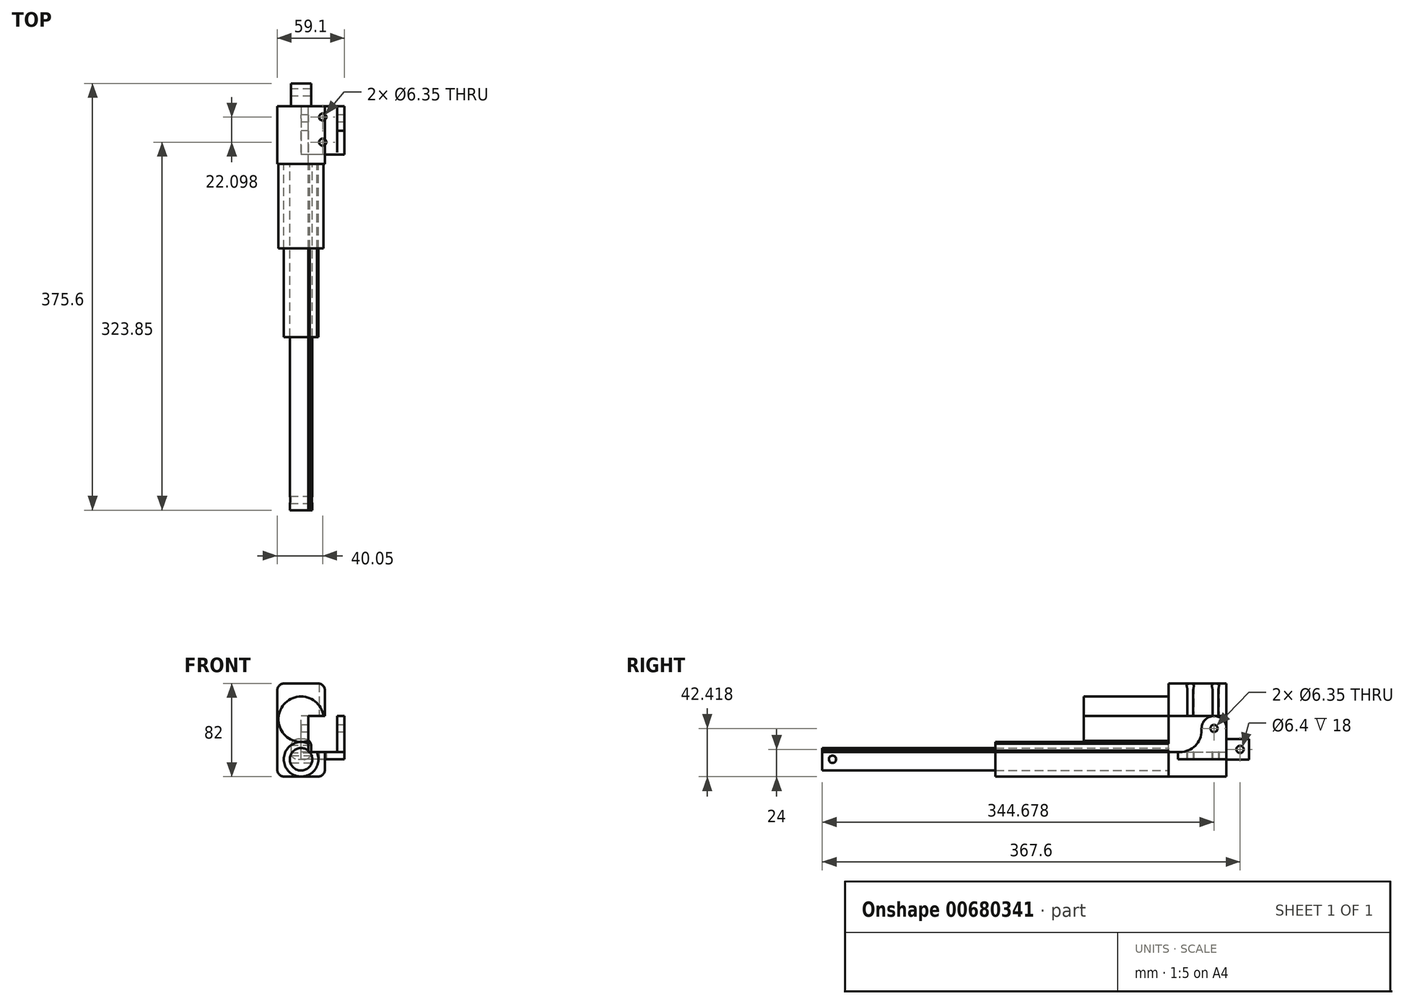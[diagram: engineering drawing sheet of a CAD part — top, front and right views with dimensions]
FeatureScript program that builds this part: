
annotation { "Feature Type Name" : "Feature", "Feature Type Description" : "" }
export const myFeature = defineFeature(function(context is Context, id is Id, definition is map)
    precondition{}
    {
        {
            var Q0;
            Q0=qCreatedBy(makeId("Front.planeOp"),FACE);
            var sketch = newSketch(context, id + "F0", { "sketchPlane" : qUnion([Q0])});
            skCircle(sketch, "E0", {"center": v(0, 0) * mm, "radius": 15.24 * mm});
            skCircle(sketch, "E1", {"center": v(0, 0) * mm, "radius": 9.9 * mm});
            skSolve(sketch);
        }
        {
            var Q0;
            Q0 = qSketchRegion(id + "F0", true);
            extrude(context, id + "F1", {"entities" : qUnion([Q0]), "depth" : 203.2 * mm, "offsetDistance" : 25.4 * mm});
        }
        {
            var Q0;
            Q0=makeQuery(id+"F1.opExtrude","CAP_FACE",FACE,{"disambiguationData":[OSD([sQuery(id+"F0.wireOp",EDGE,"E0"),sQuery(id+"F0.wireOp",EDGE,"E1")])],"isStart":true});
            var sketch = newSketch(context, id + "F2", { "sketchPlane" : qUnion([Q0])});
            skLineSegment(sketch, "E2.bottom", {"start": v(-14.65, 66.76) * mm, "end": v(14.65, 66.76) * mm});
            skLineSegment(sketch, "E2.top", {"start": v(-14.65, -15.24) * mm, "end": v(14.65, -15.24) * mm});
            skLineSegment(sketch, "E2.left", {"start": v(-21, 60.4) * mm, "end": v(-21, -8.89) * mm});
            skLineSegment(sketch, "E2.right", {"start": v(21, 60.4) * mm, "end": v(21, -8.9) * mm});
            skPoint(sketch, "E3", {"position": v(0, 66.76) * mm});
            skPoint(sketch, "E4.visualSharp", {"position": v(-21, -15.24) * mm});
            skArc(sketch, "E4.filletArc", {"start": v(-21, -8.9) * mm, "mid": v(-19.14, -13.38) * mm, "end": v(-14.65, -15.24) * mm});
            skPoint(sketch, "E5.visualSharp", {"position": v(21, -15.24) * mm});
            skArc(sketch, "E5.filletArc", {"start": v(14.65, -15.24) * mm, "mid": v(19.14, -13.38) * mm, "end": v(21, -8.9) * mm});
            skPoint(sketch, "E6.visualSharp", {"position": v(21, 66.76) * mm});
            skArc(sketch, "E6.filletArc", {"start": v(21, 60.4) * mm, "mid": v(19.14, 64.9) * mm, "end": v(14.65, 66.76) * mm});
            skPoint(sketch, "E7.visualSharp", {"position": v(-21, 66.76) * mm});
            skArc(sketch, "E7.filletArc", {"start": v(-14.65, 66.76) * mm, "mid": v(-19.14, 64.9) * mm, "end": v(-21, 60.4) * mm});
            skSolve(sketch);
        }
        {
            var Q0;
            Q0 = qSketchRegion(id + "F2", true);
            extrude(context, id + "F3", {"entities" : qUnion([Q0]), "operationType" : NewBodyOperationType.ADD, "oppositeDirection" : true, "depth" : 50.8 * mm, "offsetDistance" : 25.4 * mm});
        }
        {
            var Q0;
            Q0=makeQuery(id+"F3.boolean.opBoolean","MERGE",FACE,{"derivedFrom":[makeQuery(id+"F1.opExtrude","CAP_FACE",FACE,{"disambiguationData":[OSD([sQuery(id+"F0.wireOp",EDGE,"E0"),sQuery(id+"F0.wireOp",EDGE,"E1")])],"isStart":true}),makeQuery(id+"F3.opExtrude","CAP_FACE",FACE,{"disambiguationData":[OSD([sQuery(id+"F2.wireOp",EDGE,"E2.bottom"),sQuery(id+"F2.wireOp",EDGE,"E2.top"),sQuery(id+"F2.wireOp",EDGE,"E2.left"),sQuery(id+"F2.wireOp",EDGE,"E2.right")])],"isStart":true})]});
            var sketch = newSketch(context, id + "F4", { "sketchPlane" : qUnion([Q0])});
            skLineSegment(sketch, "E8", {"start": v(0, -15.24) * mm, "end": v(0, 66.76) * mm, "construction": true});
            skLineSegment(sketch, "E9.bottom", {"start": v(-2.65, 17.76) * mm, "end": v(2.65, 17.76) * mm});
            skLineSegment(sketch, "E9.top", {"start": v(-2.65, -0.24) * mm, "end": v(2.65, -0.24) * mm});
            skLineSegment(sketch, "E9.left", {"start": v(-9, 11.41) * mm, "end": v(-9, 6.11) * mm});
            skLineSegment(sketch, "E9.right", {"start": v(9, 11.41) * mm, "end": v(9, 6.11) * mm});
            skPoint(sketch, "E10", {"position": v(0, 17.76) * mm});
            skPoint(sketch, "E11", {"position": v(-9, 8.76) * mm});
            skPoint(sketch, "E12.visualSharp", {"position": v(-9, 17.76) * mm});
            skArc(sketch, "E12.filletArc", {"start": v(-2.65, 17.76) * mm, "mid": v(-7.14, 15.9) * mm, "end": v(-9, 11.41) * mm});
            skPoint(sketch, "E13.visualSharp", {"position": v(9, 17.76) * mm});
            skArc(sketch, "E13.filletArc", {"start": v(9, 11.41) * mm, "mid": v(7.14, 15.9) * mm, "end": v(2.65, 17.76) * mm});
            skPoint(sketch, "E14.visualSharp", {"position": v(9, -0.24) * mm});
            skArc(sketch, "E14.filletArc", {"start": v(2.65, -0.24) * mm, "mid": v(7.14, 1.62) * mm, "end": v(9, 6.11) * mm});
            skPoint(sketch, "E15.visualSharp", {"position": v(-9, -0.24) * mm});
            skArc(sketch, "E15.filletArc", {"start": v(-9, 6.11) * mm, "mid": v(-7.14, 1.62) * mm, "end": v(-2.65, -0.24) * mm});
            skSolve(sketch);
        }
        {
            var Q0;
            Q0 = qSketchRegion(id + "F4", true);
            extrude(context, id + "F5", {"entities" : qUnion([Q0]), "operationType" : NewBodyOperationType.ADD, "depth" : 20 * mm, "offsetDistance" : 25.4 * mm});
        }
        {
            var Q0;
            Q0=makeQuery(id+"F1.opExtrude","CAP_FACE",FACE,{"disambiguationData":[OSD([sQuery(id+"F0.wireOp",EDGE,"E0"),sQuery(id+"F0.wireOp",EDGE,"E1")])],"isStart":false});
            var sketch = newSketch(context, id + "F6", { "sketchPlane" : qUnion([Q0])});
            skCircle(sketch, "E16", {"center": v(0, 0) * mm, "radius": 9.9 * mm});
            skSolve(sketch);
        }
        {
            var Q0;
            Q0 = qSketchRegion(id + "F6", true);
            extrude(context, id + "F7", {"entities" : qUnion([Q0]), "depth" : 152.4 * mm, "offsetDistance" : 25.4 * mm});
        }
        {
            var Q0;
            {var subQ0=sQuery(id+"F2.wireOp",EDGE,"E2.left");var subQ1=sQuery(id+"F2.wireOp",EDGE,"E2.top");var subQ2=sQuery(id+"F2.wireOp",EDGE,"E2.bottom");var subQ3=sQuery(id+"F2.wireOp",EDGE,"E2.right");var subQ4=sQuery(id+"F2.wireOp",EDGE,"E4.filletArc");var subQ5=sQuery(id+"F2.wireOp",EDGE,"E5.filletArc");var subQ6=sQuery(id+"F2.wireOp",EDGE,"E6.filletArc");var subQ7=sQuery(id+"F2.wireOp",EDGE,"E7.filletArc");Q0=makeQuery(id+"F3.boolean.opBoolean","SPLIT",FACE,{"disambiguationData":[TD([makeQuery(id+"F1.opExtrude","SWEPT_FACE",FACE,{"disambiguationData":[OSD([sQuery(id+"F0.wireOp",EDGE,"E0")])]})])],"derivedFrom":makeQuery(id+"F3.opExtrude","CAP_FACE",FACE,{"disambiguationData":[OSD([subQ2,subQ1,subQ0,subQ3,subQ4,subQ5,subQ6,subQ7])],"isStart":false})});}
            var sketch = newSketch(context, id + "F8", { "sketchPlane" : qUnion([Q0])});
            skLineSegment(sketch, "E17", {"start": v(0, 0) * mm, "end": v(0, 110.6) * mm, "construction": true});
            skCircle(sketch, "E18", {"center": v(0, 35.24) * mm, "radius": 20 * mm});
            skSolve(sketch);
        }
        {
            var Q0;
            Q0=makeQuery(id+"F8.imprint","IMPRINT",FACE,{"disambiguationData":[TD([[makeQuery(id+"F8.imprint","IMPRINT",EDGE,{"derivedFrom":sQuery(id+"F8.wireOp",EDGE,"E18")}),1.0]])]});
            extrude(context, id + "F9", {"entities" : qUnion([Q0]), "depth" : 74.55 * mm, "offsetDistance" : 25.4 * mm});
        }
        {
            var Q0;
            Q0=makeQuery(id+"F7.opExtrude","SWEPT_FACE",FACE,{"disambiguationData":[OSD([sQuery(id+"F6.wireOp",EDGE,"E16")])]});
            cPlane(context, id + "F10", {"entities" : qUnion([Q0]), "cplaneType" : CPlaneType.LINE_ANGLE, "offset" : 25.4 * mm, "angle" : 90 * degree, "width" : 152.4 * mm, "height" : 152.4 * mm});
        }
        {
            var Q0;
            Q0=qCreatedBy(id+"F10.planeOp",FACE);
            var sketch = newSketch(context, id + "F11", { "sketchPlane" : qUnion([Q0])});
            skLineSegment(sketch, "E19", {"start": v(-355.6, 0) * mm, "end": v(-321.88, 0) * mm, "construction": true});
            skCircle(sketch, "E20", {"center": v(-346.6, 0) * mm, "radius": 3.2 * mm});
            skSolve(sketch);
        }
        {
            var Q0;
            Q0 = qSketchRegion(id + "F11", true);
            extrude(context, id + "F12", {"entities" : qUnion([Q0]), "operationType" : NewBodyOperationType.REMOVE, "endBound" : BoundingType.THROUGH_ALL, "oppositeDirection" : true, "depth" : 25.4 * mm, "offsetDistance" : 25.4 * mm, "hasSecondDirection" : true, "secondDirectionBound" : BoundingType.THROUGH_ALL, "secondDirectionOppositeDirection" : false, "secondDirectionDepth" : 25.4 * mm});
        }
        {
            var Q0;
            Q0=makeQuery(id+"F5.opExtrude","SWEPT_FACE",FACE,{"disambiguationData":[OSD([sQuery(id+"F4.wireOp",EDGE,"E9.right")])]});
            var sketch = newSketch(context, id + "F13", { "sketchPlane" : qUnion([Q0])});
            skLineSegment(sketch, "E21", {"start": v(-20, 8.76) * mm, "end": v(0, 8.76) * mm, "construction": true});
            skCircle(sketch, "E22", {"center": v(-12, 8.76) * mm, "radius": 3.2 * mm});
            skSolve(sketch);
        }
        {
            var Q0;
            Q0 = qSketchRegion(id + "F13", true);
            extrude(context, id + "F14", {"entities" : qUnion([Q0]), "operationType" : NewBodyOperationType.REMOVE, "endBound" : BoundingType.THROUGH_ALL, "oppositeDirection" : true, "depth" : 25.4 * mm, "offsetDistance" : 25.4 * mm});
        }
        {
            var Q0;
            Q0=qCreatedBy(makeId("Right.planeOp"),FACE);
            var sketch = newSketch(context, id + "F15", { "sketchPlane" : qUnion([Q0])});
            skLineSegment(sketch, "E23.bottom", {"start": v(0, 0) * mm, "end": v(-42.67, 0) * mm});
            skLineSegment(sketch, "E23.top", {"start": v(-40.9, 6.35) * mm, "end": v(-42.67, 6.35) * mm});
            skLineSegment(sketch, "E23.left", {"start": v(0, 0) * mm, "end": v(0, 27.18) * mm});
            skLineSegment(sketch, "E23.right", {"start": v(-42.67, 0) * mm, "end": v(-42.67, 6.35) * mm});
            skLineSegment(sketch, "E24.right", {"start": v(-21.84, 25.4) * mm, "end": v(-21.84, 27.18) * mm});
            skArc(sketch, "E25", {"start": v(0, 27.18) * mm, "mid": v(-10.92, 38.1) * mm, "end": v(-21.84, 27.18) * mm});
            skArc(sketch, "E26.filletArc", {"start": v(-40.9, 6.35) * mm, "mid": v(-27.42, 11.93) * mm, "end": v(-21.84, 25.4) * mm});
            skCircle(sketch, "E27", {"center": v(-10.92, 27.18) * mm, "radius": 3.18 * mm});
            skSolve(sketch);
        }
        {
            var Q0;
            Q0 = qSketchRegion(id + "F15", true);
            extrude(context, id + "F16", {"entities" : qUnion([Q0]), "depth" : 38.1 * mm, "offsetDistance" : 25.4 * mm});
        }
        {
            var Q0;
            Q0=makeQuery(id+"F16.opExtrude","SWEPT_FACE",FACE,{"disambiguationData":[OSD([sQuery(id+"F15.wireOp",EDGE,"E23.left")])]});
            var sketch = newSketch(context, id + "F17", { "sketchPlane" : qUnion([Q0])});
            skLineSegment(sketch, "E28", {"start": v(0, 6.35) * mm, "end": v(-38.1, 6.35) * mm, "construction": true});
            skLineSegment(sketch, "E29.bottom", {"start": v(-31.75, 6.35) * mm, "end": v(-6.35, 6.35) * mm});
            skLineSegment(sketch, "E29.top", {"start": v(-31.75, 38.1) * mm, "end": v(-6.35, 38.1) * mm});
            skLineSegment(sketch, "E29.left", {"start": v(-31.75, 6.35) * mm, "end": v(-31.75, 38.1) * mm});
            skLineSegment(sketch, "E29.right", {"start": v(-6.35, 6.35) * mm, "end": v(-6.35, 38.1) * mm});
            skPoint(sketch, "E30", {"position": v(-19.05, 6.35) * mm});
            skLineSegment(sketch, "E31", {"start": v(-19.05, 6.35) * mm, "end": v(-19.05, 40.65) * mm, "construction": true});
            skPoint(sketch, "E32", {"position": v(-19.05, 38.1) * mm});
            skSolve(sketch);
        }
        {
            var Q0;
            Q0 = qSketchRegion(id + "F17", true);
            extrude(context, id + "F18", {"entities" : qUnion([Q0]), "operationType" : NewBodyOperationType.REMOVE, "endBound" : BoundingType.THROUGH_ALL, "oppositeDirection" : true, "depth" : 25.4 * mm, "offsetDistance" : 25.4 * mm});
        }
        {
            var Q0;
            Q0=makeQuery(id+"F16.opExtrude","SWEPT_FACE",FACE,{"disambiguationData":[OSD([sQuery(id+"F15.wireOp",EDGE,"E23.bottom")])]});
            var sketch = newSketch(context, id + "F19", { "sketchPlane" : qUnion([Q0])});
            skLineSegment(sketch, "E33", {"start": v(19.05, 0) * mm, "end": v(19.05, 42.67) * mm, "construction": true});
            skLineSegment(sketch, "E34", {"start": v(0, 21.34) * mm, "end": v(38.1, 21.34) * mm, "construction": true});
            skCircle(sketch, "E35", {"center": v(19.05, 9.65) * mm, "radius": 3.18 * mm});
            skCircle(sketch, "E36", {"center": v(19.05, 31.75) * mm, "radius": 3.18 * mm});
            skSolve(sketch);
        }
        {
            var Q0;
            Q0 = qSketchRegion(id + "F19", true);
            extrude(context, id + "F20", {"entities" : qUnion([Q0]), "operationType" : NewBodyOperationType.REMOVE, "endBound" : BoundingType.THROUGH_ALL, "oppositeDirection" : true, "depth" : 25.4 * mm, "offsetDistance" : 25.4 * mm});
        }
    });
